# Revit family: M200-A160 DAWSxxxESGS
name_source: partatom
category: Leuchten
units: mm (PartAtom-declared; Revit-internal decimal feet)

## family parameters
Basisbauteil = Fläche
Beim Laden mit Abzugskörper schneiden = Nein
Bemaßung runder Anschluss = Durchmesser verwenden
Gemeinsam genutzt = Nein
Lichtquelle = Ja
OmniClass-Nummer = 23.80.70.11
OmniClass-Titel = Luminaries for Internal Lighting
Raumberechnungspunkt = Nein
Teiletyp = Normal

## types (4) — shared parameters
Baugruppenkennzeichen = D5020200
Datei für fotometrisches Netz = M200-A_ESGS.IES
Emissionsform beim Rendern sichtbar = Nein
Farbfilter = 16777215
Farbtemperaturverschiebung bei Dämpfen der Lampe = <Keine Auswahl>
Hersteller = RIDI Leuchten GmbH
Lampe = LED
Neigungswinkel = 90.00°
Scheinlast = 44 VA
URL = www.ridi.de
Von Breite des Rechtecks ausssenden = 1448 mm  [stored 4.75066 ft]
Von Länge des Rechtecks aussenden = 151 mm  [stored 0.495407 ft]
brand = RIDI
conformity mark = CE
electrical safety class = 2
height = 70 mm  [stored 0.229659 ft]
ingress protection (IP) code = IP65
length = 1600 mm  [stored 5.24934 ft]
nominal frequency = 50-60Hz
nominal voltage = 230
rated input power = 44
voltage type (AC, DC, UC) = AC
weight = 12,5
width = 200 mm  [stored 0.656168 ft]
zero-valued in all types: Vorgabe-Ansicht

## per-type parameters (varying)
| type | Modell |
| M200-A160 DAWS830ESGS0550 | 0637618 |
| M200-A160 DAWS840ESGS0550 | 0637619 |
| M200-A160 NDWS830ESGS0550-RF | 0627618 |
| M200-A160 NDWS840ESGS0550-RF | 0627619 |

note: column(s) folded — value = type name in every type: product name

note: [stored X ft] marks values corroborated as IEEE doubles in the binary element streams (Revit-internal decimal feet)
